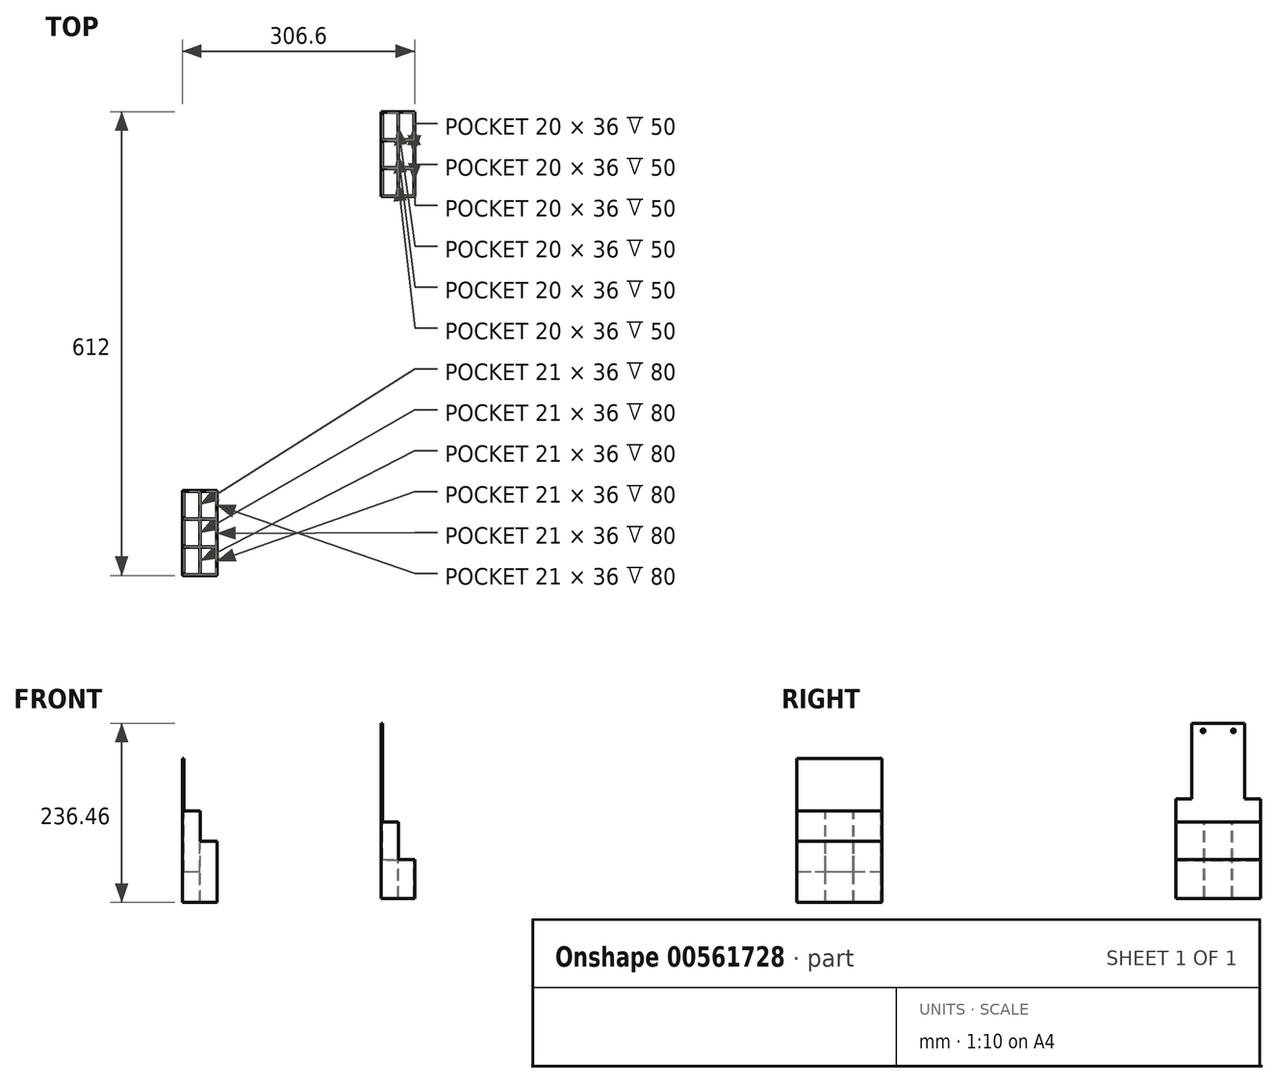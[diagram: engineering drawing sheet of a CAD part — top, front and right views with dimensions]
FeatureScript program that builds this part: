
annotation { "Feature Type Name" : "Feature", "Feature Type Description" : "" }
export const myFeature = defineFeature(function(context is Context, id is Id, definition is map)
    precondition{}
    {
        {
            var Q0;
            Q0=qCreatedBy(makeId("Front.planeOp"),FACE);
            var sketch = newSketch(context, id + "F0", { "sketchPlane" : qUnion([Q0])});
            skLineSegment(sketch, "E0", {"start": v(-58.57, 112.66) * mm, "end": v(-58.57, -77.34) * mm});
            skLineSegment(sketch, "E1", {"start": v(-58.57, -77.34) * mm, "end": v(-12.57, -77.34) * mm});
            skLineSegment(sketch, "E2", {"start": v(-12.57, -77.34) * mm, "end": v(-12.57, 3.66) * mm});
            skLineSegment(sketch, "E3", {"start": v(-12.57, 3.66) * mm, "end": v(-34.57, 3.66) * mm});
            skLineSegment(sketch, "E4", {"start": v(-34.57, 3.66) * mm, "end": v(-34.57, 43.66) * mm});
            skLineSegment(sketch, "E5", {"start": v(-34.57, 43.66) * mm, "end": v(-56.57, 43.66) * mm});
            skLineSegment(sketch, "E6", {"start": v(-56.57, 43.66) * mm, "end": v(-56.57, 112.66) * mm});
            skLineSegment(sketch, "E7", {"start": v(-58.57, 112.66) * mm, "end": v(-56.57, 112.66) * mm});
            skSolve(sketch);
        }
        {
            var Q0;
            Q0=makeQuery(id+"F0.imprint","IMPRINT",FACE,{"disambiguationData":[TD([[makeQuery(id+"F0.imprint","IMPRINT",EDGE,{"derivedFrom":sQuery(id+"F0.wireOp",EDGE,"E0")}),1.0]])]});
            extrude(context, id + "F1", {"entities" : qUnion([Q0]), "depth" : 112 * mm, "offsetDistance" : 25 * mm});
        }
        {
            var Q0;
            Q0=makeQuery(id+"F1.opExtrude","SWEPT_FACE",FACE,{"disambiguationData":[OSD([sQuery(id+"F0.wireOp",EDGE,"E5")])]});
            var sketch = newSketch(context, id + "F2", { "sketchPlane" : qUnion([Q0])});
            skLineSegment(sketch, "E8.bottom", {"start": v(-56.57, -1) * mm, "end": v(-35.57, -1) * mm});
            skLineSegment(sketch, "E8.top", {"start": v(-56.57, -37) * mm, "end": v(-35.57, -37) * mm});
            skLineSegment(sketch, "E8.left", {"start": v(-56.57, -1) * mm, "end": v(-56.57, -37) * mm});
            skLineSegment(sketch, "E8.right", {"start": v(-35.57, -1) * mm, "end": v(-35.57, -37) * mm});
            skLineSegment(sketch, "E9.bottom", {"start": v(-56.57, -38) * mm, "end": v(-35.57, -38) * mm});
            skLineSegment(sketch, "E9.top", {"start": v(-56.57, -74) * mm, "end": v(-35.57, -74) * mm});
            skLineSegment(sketch, "E9.left", {"start": v(-56.57, -38) * mm, "end": v(-56.57, -74) * mm});
            skLineSegment(sketch, "E9.right", {"start": v(-35.57, -38) * mm, "end": v(-35.57, -74) * mm});
            skLineSegment(sketch, "E10.bottom", {"start": v(-56.57, -75) * mm, "end": v(-35.57, -75) * mm});
            skLineSegment(sketch, "E10.top", {"start": v(-56.57, -111) * mm, "end": v(-35.57, -111) * mm});
            skLineSegment(sketch, "E10.left", {"start": v(-56.57, -75) * mm, "end": v(-56.57, -111) * mm});
            skLineSegment(sketch, "E10.right", {"start": v(-35.57, -75) * mm, "end": v(-35.57, -111) * mm});
            skSolve(sketch);
        }
        {
            var Q0;
            Q0=makeQuery(id+"F2.imprint","IMPRINT",FACE,{"disambiguationData":[TD([[makeQuery(id+"F2.imprint","IMPRINT",EDGE,{"derivedFrom":sQuery(id+"F2.wireOp",EDGE,"E10.bottom")}),-1.0]])]});
            var Q1;
            Q1=makeQuery(id+"F2.imprint","IMPRINT",FACE,{"disambiguationData":[TD([[makeQuery(id+"F2.imprint","IMPRINT",EDGE,{"derivedFrom":sQuery(id+"F2.wireOp",EDGE,"E9.bottom")}),-1.0]])]});
            var Q2;
            Q2=makeQuery(id+"F2.imprint","IMPRINT",FACE,{"disambiguationData":[TD([[makeQuery(id+"F2.imprint","IMPRINT",EDGE,{"derivedFrom":sQuery(id+"F2.wireOp",EDGE,"E8.bottom")}),-1.0]])]});
            extrude(context, id + "F3", {"entities" : qUnion([Q0, Q1, Q2]), "operationType" : NewBodyOperationType.REMOVE, "oppositeDirection" : true, "depth" : 80 * mm, "offsetDistance" : 25 * mm});
        }
        {
            var Q0;
            Q0=makeQuery(id+"F1.opExtrude","SWEPT_FACE",FACE,{"disambiguationData":[OSD([sQuery(id+"F0.wireOp",EDGE,"E3")])]});
            var sketch = newSketch(context, id + "F4", { "sketchPlane" : qUnion([Q0])});
            skLineSegment(sketch, "E11.0", {"start": v(-34.57, -112) * mm, "end": v(-34.57, 0) * mm, "construction": true});
            skLineSegment(sketch, "E12.bottom", {"start": v(-34.57, -1) * mm, "end": v(-13.57, -1) * mm});
            skLineSegment(sketch, "E12.top", {"start": v(-34.57, -37) * mm, "end": v(-13.57, -37) * mm});
            skLineSegment(sketch, "E12.left", {"start": v(-34.57, -1) * mm, "end": v(-34.57, -37) * mm});
            skLineSegment(sketch, "E12.right", {"start": v(-13.57, -1) * mm, "end": v(-13.57, -37) * mm});
            skLineSegment(sketch, "E13.bottom", {"start": v(-34.57, -38) * mm, "end": v(-13.57, -38) * mm});
            skLineSegment(sketch, "E13.top", {"start": v(-34.57, -74) * mm, "end": v(-13.57, -74) * mm});
            skLineSegment(sketch, "E13.left", {"start": v(-34.57, -38) * mm, "end": v(-34.57, -74) * mm});
            skLineSegment(sketch, "E13.right", {"start": v(-13.57, -38) * mm, "end": v(-13.57, -74) * mm});
            skLineSegment(sketch, "E14.bottom", {"start": v(-34.57, -75) * mm, "end": v(-13.57, -75) * mm});
            skLineSegment(sketch, "E14.top", {"start": v(-34.57, -111) * mm, "end": v(-13.57, -111) * mm});
            skLineSegment(sketch, "E14.left", {"start": v(-34.57, -75) * mm, "end": v(-34.57, -111) * mm});
            skLineSegment(sketch, "E14.right", {"start": v(-13.57, -75) * mm, "end": v(-13.57, -111) * mm});
            skSolve(sketch);
        }
        {
            var Q0;
            Q0=makeQuery(id+"F4.imprint","IMPRINT",FACE,{"disambiguationData":[TD([[makeQuery(id+"F4.imprint","IMPRINT",EDGE,{"derivedFrom":sQuery(id+"F4.wireOp",EDGE,"E12.bottom")}),-1.0]])]});
            var Q1;
            Q1=makeQuery(id+"F4.imprint","IMPRINT",FACE,{"disambiguationData":[TD([[makeQuery(id+"F4.imprint","IMPRINT",EDGE,{"derivedFrom":sQuery(id+"F4.wireOp",EDGE,"E13.bottom")}),-1.0]])]});
            var Q2;
            Q2=makeQuery(id+"F4.imprint","IMPRINT",FACE,{"disambiguationData":[TD([[makeQuery(id+"F4.imprint","IMPRINT",EDGE,{"derivedFrom":sQuery(id+"F4.wireOp",EDGE,"E14.bottom")}),-1.0]])]});
            extrude(context, id + "F5", {"entities" : qUnion([Q0, Q1, Q2]), "operationType" : NewBodyOperationType.REMOVE, "oppositeDirection" : true, "depth" : 80 * mm, "offsetDistance" : 25 * mm});
        }
        {
            var Q0;
            Q0=makeQuery(id+"F1.opExtrude","SWEPT_FACE",FACE,{"disambiguationData":[OSD([sQuery(id+"F0.wireOp",EDGE,"E0")])]});
            var sketch = newSketch(context, id + "F6", { "sketchPlane" : qUnion([Q0])});
            skLineSegment(sketch, "E15.bottom", {"start": v(1, -77.34) * mm, "end": v(111, -77.34) * mm});
            skLineSegment(sketch, "E15.top", {"start": v(1, -37.34) * mm, "end": v(111, -37.34) * mm});
            skLineSegment(sketch, "E15.left", {"start": v(1, -77.34) * mm, "end": v(1, -37.34) * mm});
            skLineSegment(sketch, "E15.right", {"start": v(111, -77.34) * mm, "end": v(111, -37.34) * mm});
            skSolve(sketch);
        }
        {
            var Q0;
            Q0=makeQuery(id+"F6.imprint","IMPRINT",FACE,{"disambiguationData":[TD([[makeQuery(id+"F6.imprint","IMPRINT",EDGE,{"derivedFrom":sQuery(id+"F6.wireOp",EDGE,"E15.bottom")}),-1.0]])]});
            extrude(context, id + "F7", {"entities" : qUnion([Q0]), "operationType" : NewBodyOperationType.REMOVE, "oppositeDirection" : true, "depth" : 23 * mm, "offsetDistance" : 25 * mm});
        }
        {
            var Q0;
            Q0=makeQuery(id+"F1.opExtrude","SWEPT_BODY",BODY,{"disambiguationData":[OSD([sQuery(id+"F0.wireOp",EDGE,"E0"),sQuery(id+"F0.wireOp",EDGE,"E1"),sQuery(id+"F0.wireOp",EDGE,"E2"),sQuery(id+"F0.wireOp",EDGE,"E3"),sQuery(id+"F0.wireOp",EDGE,"E4"),sQuery(id+"F0.wireOp",EDGE,"E5"),sQuery(id+"F0.wireOp",EDGE,"E6"),sQuery(id+"F0.wireOp",EDGE,"E7")])]});
            transform(context, id + "F8", {"entities" : qUnion([Q0]), "transformType" : TransformType.TRANSLATION_3D, "dx" : 0 * mm, "dy" : 1000 * mm, "dz" : 0 * mm, "makeCopy" : true});
        }
        {
            var Q0;
            Q0=makeQuery(id+"F8.opPattern","COPY",BODY,{"derivedFrom":makeQuery(id+"F1.opExtrude","SWEPT_BODY",BODY,{"disambiguationData":[OSD([sQuery(id+"F0.wireOp",EDGE,"E0"),sQuery(id+"F0.wireOp",EDGE,"E1"),sQuery(id+"F0.wireOp",EDGE,"E2"),sQuery(id+"F0.wireOp",EDGE,"E3"),sQuery(id+"F0.wireOp",EDGE,"E4"),sQuery(id+"F0.wireOp",EDGE,"E5"),sQuery(id+"F0.wireOp",EDGE,"E6"),sQuery(id+"F0.wireOp",EDGE,"E7")])]}),"instanceName":"1"});
            deleteBodies(context, id + "F9", {"entities" : qUnion([Q0])});
        }
        {
            var Q0;
            Q0=qCreatedBy(makeId("Front.planeOp"),FACE);
            var sketch = newSketch(context, id + "F10", { "sketchPlane" : qUnion([Q0])});
            skLineSegment(sketch, "E16", {"start": v(204.03, -71.88) * mm, "end": v(248.03, -71.88) * mm});
            skLineSegment(sketch, "E17", {"start": v(248.03, -71.88) * mm, "end": v(248.03, -20.88) * mm});
            skLineSegment(sketch, "E18", {"start": v(248.03, -20.88) * mm, "end": v(227.03, -20.88) * mm});
            skLineSegment(sketch, "E19", {"start": v(227.03, -20.88) * mm, "end": v(227.03, 29.12) * mm});
            skLineSegment(sketch, "E20", {"start": v(227.03, 29.12) * mm, "end": v(206.03, 29.12) * mm});
            skLineSegment(sketch, "E21", {"start": v(206.03, 29.12) * mm, "end": v(206.03, 159.12) * mm});
            skLineSegment(sketch, "E22", {"start": v(206.03, 159.12) * mm, "end": v(204.03, 159.12) * mm});
            skLineSegment(sketch, "E23", {"start": v(204.03, 159.12) * mm, "end": v(204.03, -71.88) * mm});
            skSolve(sketch);
        }
        {
            var Q0;
            Q0=makeQuery(id+"F10.imprint","IMPRINT",FACE,{"disambiguationData":[TD([[makeQuery(id+"F10.imprint","IMPRINT",EDGE,{"derivedFrom":sQuery(id+"F10.wireOp",EDGE,"E16")}),1.0]])]});
            extrude(context, id + "F11", {"entities" : qUnion([Q0]), "depth" : 112 * mm, "offsetDistance" : 25 * mm});
        }
        {
            var Q0;
            Q0=makeQuery(id+"F11.opExtrude","SWEPT_FACE",FACE,{"disambiguationData":[OSD([sQuery(id+"F10.wireOp",EDGE,"E18")])]});
            var sketch = newSketch(context, id + "F12", { "sketchPlane" : qUnion([Q0])});
            skLineSegment(sketch, "E24.0", {"start": v(248.03, -112) * mm, "end": v(227.03, -112) * mm});
            skLineSegment(sketch, "E25.0", {"start": v(248.03, -112) * mm, "end": v(248.03, 0) * mm});
            skLineSegment(sketch, "E26", {"start": v(227.03, -111) * mm, "end": v(247.03, -111) * mm});
            skLineSegment(sketch, "E27", {"start": v(247.03, -111) * mm, "end": v(247.03, -75) * mm});
            skLineSegment(sketch, "E28", {"start": v(247.03, -75) * mm, "end": v(227.03, -75) * mm});
            skLineSegment(sketch, "E29", {"start": v(227.03, -75) * mm, "end": v(227.03, -74) * mm});
            skLineSegment(sketch, "E30", {"start": v(227.03, -74) * mm, "end": v(247.03, -74) * mm});
            skLineSegment(sketch, "E31", {"start": v(247.03, -74) * mm, "end": v(247.03, -38) * mm});
            skLineSegment(sketch, "E32", {"start": v(247.03, -38) * mm, "end": v(227.03, -38) * mm});
            skLineSegment(sketch, "E33", {"start": v(227.03, -111) * mm, "end": v(227.03, -75) * mm});
            skLineSegment(sketch, "E34", {"start": v(227.03, -74) * mm, "end": v(227.03, -38) * mm});
            skLineSegment(sketch, "E35.bottom", {"start": v(227.03, -37) * mm, "end": v(247.03, -37) * mm});
            skLineSegment(sketch, "E35.top", {"start": v(227.03, -1) * mm, "end": v(247.03, -1) * mm});
            skLineSegment(sketch, "E35.left", {"start": v(227.03, -37) * mm, "end": v(227.03, -1) * mm});
            skLineSegment(sketch, "E35.right", {"start": v(247.03, -37) * mm, "end": v(247.03, -1) * mm});
            skSolve(sketch);
        }
        {
            var Q0;
            Q0=makeQuery(id+"F12.imprint","IMPRINT",FACE,{"disambiguationData":[TD([[makeQuery(id+"F12.imprint","IMPRINT",EDGE,{"derivedFrom":sQuery(id+"F12.wireOp",EDGE,"E30")}),1.0]])]});
            var Q1;
            Q1=makeQuery(id+"F12.imprint","IMPRINT",FACE,{"disambiguationData":[TD([[makeQuery(id+"F12.imprint","IMPRINT",EDGE,{"derivedFrom":sQuery(id+"F12.wireOp",EDGE,"E26")}),1.0]])]});
            var Q2;
            Q2=makeQuery(id+"F12.imprint","IMPRINT",FACE,{"disambiguationData":[TD([[makeQuery(id+"F12.imprint","IMPRINT",EDGE,{"derivedFrom":sQuery(id+"F12.wireOp",EDGE,"E35.bottom")}),1.0]])]});
            extrude(context, id + "F13", {"entities" : qUnion([Q0, Q1, Q2]), "operationType" : NewBodyOperationType.REMOVE, "oppositeDirection" : true, "depth" : 50 * mm, "offsetDistance" : 25 * mm});
        }
        {
            var Q0;
            Q0=makeQuery(id+"F11.opExtrude","SWEPT_FACE",FACE,{"disambiguationData":[OSD([sQuery(id+"F10.wireOp",EDGE,"E20")])]});
            var sketch = newSketch(context, id + "F14", { "sketchPlane" : qUnion([Q0])});
            skLineSegment(sketch, "E36.0", {"start": v(227.03, -112) * mm, "end": v(206.03, -112) * mm});
            skLineSegment(sketch, "E36.1", {"start": v(206.03, -112) * mm, "end": v(206.03, 0) * mm});
            skLineSegment(sketch, "E37.bottom", {"start": v(206.03, -111) * mm, "end": v(226.03, -111) * mm});
            skLineSegment(sketch, "E37.top", {"start": v(206.03, -75) * mm, "end": v(226.03, -75) * mm});
            skLineSegment(sketch, "E37.left", {"start": v(206.03, -111) * mm, "end": v(206.03, -75) * mm});
            skLineSegment(sketch, "E37.right", {"start": v(226.03, -111) * mm, "end": v(226.03, -75) * mm});
            skLineSegment(sketch, "E38.bottom", {"start": v(206.03, -74) * mm, "end": v(226.03, -74) * mm});
            skLineSegment(sketch, "E38.top", {"start": v(206.03, -38) * mm, "end": v(226.03, -38) * mm});
            skLineSegment(sketch, "E38.left", {"start": v(206.03, -74) * mm, "end": v(206.03, -38) * mm});
            skLineSegment(sketch, "E38.right", {"start": v(226.03, -74) * mm, "end": v(226.03, -38) * mm});
            skLineSegment(sketch, "E39.bottom", {"start": v(206.03, -37) * mm, "end": v(226.03, -37) * mm});
            skLineSegment(sketch, "E39.top", {"start": v(206.03, -1) * mm, "end": v(226.03, -1) * mm});
            skLineSegment(sketch, "E39.left", {"start": v(206.03, -37) * mm, "end": v(206.03, -1) * mm});
            skLineSegment(sketch, "E39.right", {"start": v(226.03, -37) * mm, "end": v(226.03, -1) * mm});
            skLineSegment(sketch, "E40", {"start": v(206.03, -1) * mm, "end": v(206.03, -37) * mm});
            skLineSegment(sketch, "E41", {"start": v(206.03, -38) * mm, "end": v(206.03, -74) * mm});
            skLineSegment(sketch, "E42", {"start": v(206.03, -75) * mm, "end": v(206.03, -111) * mm});
            skSolve(sketch);
        }
        {
            var Q0;
            Q0=makeQuery(id+"F14.imprint","IMPRINT",FACE,{"disambiguationData":[TD([[makeQuery(id+"F14.imprint","IMPRINT",EDGE,{"derivedFrom":sQuery(id+"F14.wireOp",EDGE,"E37.bottom")}),1.0]])]});
            var Q1;
            Q1=makeQuery(id+"F14.imprint","IMPRINT",FACE,{"disambiguationData":[TD([[makeQuery(id+"F14.imprint","IMPRINT",EDGE,{"derivedFrom":sQuery(id+"F14.wireOp",EDGE,"E38.bottom")}),1.0]])]});
            var Q2;
            Q2=makeQuery(id+"F14.imprint","IMPRINT",FACE,{"disambiguationData":[TD([[makeQuery(id+"F14.imprint","IMPRINT",EDGE,{"derivedFrom":sQuery(id+"F14.wireOp",EDGE,"E39.bottom")}),1.0]])]});
            extrude(context, id + "F15", {"entities" : qUnion([Q0, Q1, Q2]), "operationType" : NewBodyOperationType.REMOVE, "oppositeDirection" : true, "depth" : 50 * mm, "offsetDistance" : 25 * mm});
        }
        {
            var Q0;
            Q0=makeQuery(id+"F11.opExtrude","SWEPT_FACE",FACE,{"disambiguationData":[OSD([sQuery(id+"F10.wireOp",EDGE,"E23")])]});
            var sketch = newSketch(context, id + "F16", { "sketchPlane" : qUnion([Q0])});
            skLineSegment(sketch, "E43.bottom", {"start": v(111, -71.88) * mm, "end": v(1, -71.88) * mm});
            skLineSegment(sketch, "E43.top", {"start": v(111, -21.88) * mm, "end": v(1, -21.88) * mm});
            skLineSegment(sketch, "E43.left", {"start": v(111, -71.88) * mm, "end": v(111, -21.88) * mm});
            skLineSegment(sketch, "E43.right", {"start": v(1, -71.88) * mm, "end": v(1, -21.88) * mm});
            skSolve(sketch);
        }
        {
            var Q0;
            Q0=makeQuery(id+"F16.imprint","IMPRINT",FACE,{"disambiguationData":[TD([[makeQuery(id+"F16.imprint","IMPRINT",EDGE,{"derivedFrom":sQuery(id+"F16.wireOp",EDGE,"E43.bottom")}),-1.0]])]});
            extrude(context, id + "F17", {"entities" : qUnion([Q0]), "operationType" : NewBodyOperationType.REMOVE, "oppositeDirection" : true, "depth" : 22 * mm, "offsetDistance" : 25 * mm});
        }
        {
            var Q0;
            Q0=makeQuery(id+"F15.boolean.opBoolean","MERGE",FACE,{"derivedFrom":[makeQuery(id+"F11.opExtrude","SWEPT_FACE",FACE,{"disambiguationData":[OSD([sQuery(id+"F10.wireOp",EDGE,"E21")])]}),makeQuery(id+"F15.opExtrude","SWEPT_FACE",FACE,{"disambiguationData":[OSD([sQuery(id+"F14.wireOp",EDGE,"E40")])]}),makeQuery(id+"F15.opExtrude","SWEPT_FACE",FACE,{"disambiguationData":[OSD([sQuery(id+"F14.wireOp",EDGE,"E41")])]}),makeQuery(id+"F15.opExtrude","SWEPT_FACE",FACE,{"disambiguationData":[OSD([sQuery(id+"F14.wireOp",EDGE,"E42")])]})]});
            var sketch = newSketch(context, id + "F18", { "sketchPlane" : qUnion([Q0])});
            skLineSegment(sketch, "E44.0", {"start": v(0, 29.12) * mm, "end": v(0, 159.12) * mm, "construction": true});
            skLineSegment(sketch, "E45.bottom", {"start": v(0, 159.12) * mm, "end": v(-21, 159.12) * mm});
            skLineSegment(sketch, "E45.top", {"start": v(0, 59.12) * mm, "end": v(-21, 59.12) * mm});
            skLineSegment(sketch, "E45.left", {"start": v(0, 159.12) * mm, "end": v(0, 59.12) * mm});
            skLineSegment(sketch, "E45.right", {"start": v(-21, 159.12) * mm, "end": v(-21, 59.12) * mm});
            skLineSegment(sketch, "E46.0", {"start": v(-112, 29.12) * mm, "end": v(-112, 159.12) * mm, "construction": true});
            skLineSegment(sketch, "E47.bottom", {"start": v(-112, 159.12) * mm, "end": v(-91, 159.12) * mm});
            skLineSegment(sketch, "E47.top", {"start": v(-112, 59.12) * mm, "end": v(-91, 59.12) * mm});
            skLineSegment(sketch, "E47.left", {"start": v(-112, 159.12) * mm, "end": v(-112, 59.12) * mm});
            skLineSegment(sketch, "E47.right", {"start": v(-91, 159.12) * mm, "end": v(-91, 59.12) * mm});
            skLineSegment(sketch, "E48", {"start": v(-91, 149.12) * mm, "end": v(-21, 149.12) * mm, "construction": true});
            skLineSegment(sketch, "E49", {"start": v(-76, 95.4) * mm, "end": v(-76, 148.5) * mm, "construction": true});
            skLineSegment(sketch, "E50", {"start": v(-36, 95.8) * mm, "end": v(-36, 148.25) * mm, "construction": true});
            skCircle(sketch, "E51", {"center": v(-76, 149.12) * mm, "radius": 2.5 * mm});
            skCircle(sketch, "E52", {"center": v(-36, 149.12) * mm, "radius": 2.5 * mm});
            skSolve(sketch);
        }
        {
            var Q0;
            Q0=makeQuery(id+"F18.imprint","IMPRINT",FACE,{"disambiguationData":[TD([[makeQuery(id+"F18.imprint","IMPRINT",EDGE,{"derivedFrom":sQuery(id+"F18.wireOp",EDGE,"E47.bottom")}),-1.0]])]});
            var Q1;
            Q1=makeQuery(id+"F18.imprint","IMPRINT",FACE,{"disambiguationData":[TD([[makeQuery(id+"F18.imprint","IMPRINT",EDGE,{"derivedFrom":sQuery(id+"F18.wireOp",EDGE,"E45.bottom")}),-1.0]])]});
            extrude(context, id + "F19", {"entities" : qUnion([Q0, Q1]), "operationType" : NewBodyOperationType.REMOVE, "endBound" : BoundingType.UP_TO_NEXT, "oppositeDirection" : true, "depth" : 25 * mm, "offsetDistance" : 25 * mm});
        }
        {
            var Q0;
            Q0=makeQuery(id+"F18.imprint","IMPRINT",FACE,{"disambiguationData":[TD([[makeQuery(id+"F18.imprint","IMPRINT",EDGE,{"derivedFrom":sQuery(id+"F18.wireOp",EDGE,"E51")}),1.0]])]});
            var Q1;
            Q1=makeQuery(id+"F18.imprint","IMPRINT",FACE,{"disambiguationData":[TD([[makeQuery(id+"F18.imprint","IMPRINT",EDGE,{"derivedFrom":sQuery(id+"F18.wireOp",EDGE,"E52")}),1.0]])]});
            var Q2;
            Q2=sQuery(id+"F18.wireOp",EDGE,"E51");
            var Q3;
            Q3=sQuery(id+"F18.wireOp",EDGE,"E52");
            extrude(context, id + "F20", {"entities" : qUnion([Q0, Q1]), "operationType" : NewBodyOperationType.REMOVE, "surfaceEntities" : qUnion([Q2, Q3]), "endBound" : BoundingType.UP_TO_NEXT, "oppositeDirection" : true, "depth" : 25 * mm, "offsetDistance" : 25 * mm});
        }
        {
            var Q0;
            Q0=makeQuery(id+"F11.opExtrude","SWEPT_BODY",BODY,{"disambiguationData":[OSD([sQuery(id+"F10.wireOp",EDGE,"E16"),sQuery(id+"F10.wireOp",EDGE,"E17"),sQuery(id+"F10.wireOp",EDGE,"E18"),sQuery(id+"F10.wireOp",EDGE,"E19"),sQuery(id+"F10.wireOp",EDGE,"E20"),sQuery(id+"F10.wireOp",EDGE,"E21"),sQuery(id+"F10.wireOp",EDGE,"E22"),sQuery(id+"F10.wireOp",EDGE,"E23")])]});
            transform(context, id + "F21", {"entities" : qUnion([Q0]), "transformType" : TransformType.TRANSLATION_3D, "dx" : 0 * mm, "dy" : 500 * mm, "dz" : 0 * mm, "makeCopy" : false});
        }
    });
